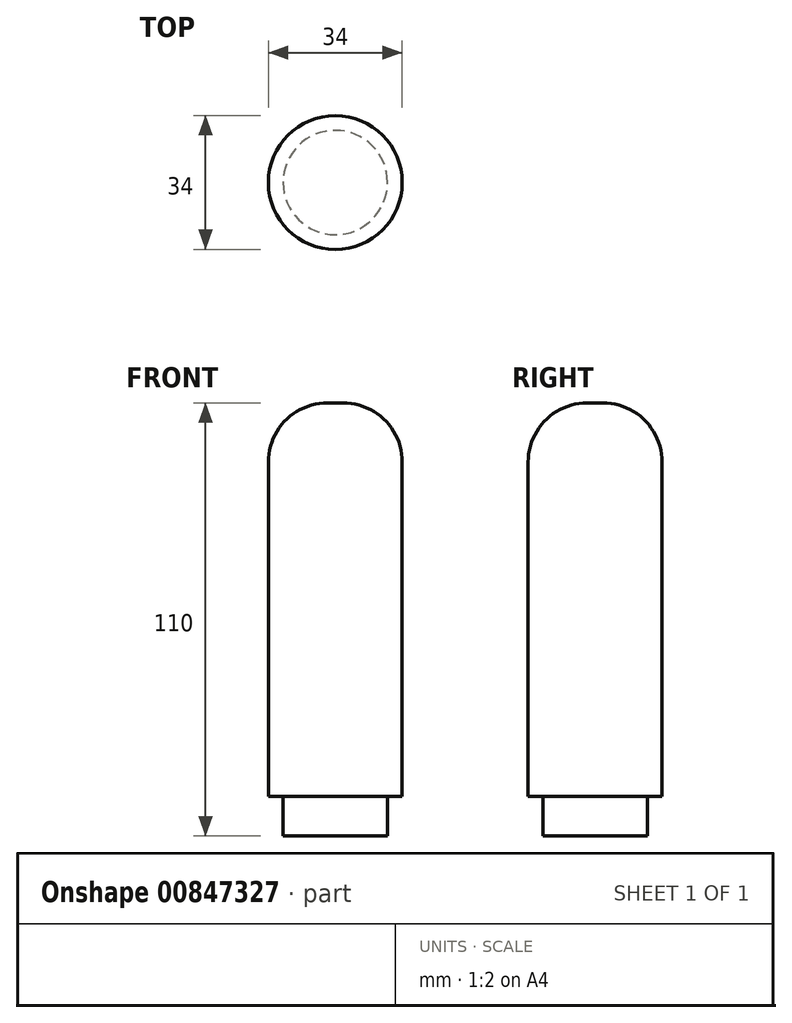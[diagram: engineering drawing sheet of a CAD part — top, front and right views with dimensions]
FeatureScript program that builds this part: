
annotation { "Feature Type Name" : "Feature", "Feature Type Description" : "" }
export const myFeature = defineFeature(function(context is Context, id is Id, definition is map)
    precondition{}
    {
        {
            var Q0;
            Q0=qCreatedBy(makeId("Top.planeOp"),FACE);
            var sketch = newSketch(context, id + "F0", { "sketchPlane" : qUnion([Q0])});
            skCircle(sketch, "E0", {"center": v(0, 0) * mm, "radius": 13.25 * mm});
            skCircle(sketch, "E1", {"center": v(0, 0) * mm, "radius": 17 * mm});
            skCircle(sketch, "E2", {"center": v(0, 0) * mm, "radius": 10.25 * mm});
            skSolve(sketch);
        }
        {
            var Q0;
            Q0 = qSketchRegion(id + "F0", true);
            var Q1;
            Q1=makeQuery(id+"F0.imprint","IMPRINT",FACE,{"disambiguationData":[TD([[makeQuery(id+"F0.imprint","IMPRINT",EDGE,{"derivedFrom":sQuery(id+"F0.wireOp",EDGE,"E0")}),1.0]])]});
            var Q2;
            Q2=makeQuery(id+"F0.imprint","IMPRINT",FACE,{"disambiguationData":[TD([[makeQuery(id+"F0.imprint","IMPRINT",EDGE,{"derivedFrom":sQuery(id+"F0.wireOp",EDGE,"E2")}),1.0]])]});
            extrude(context, id + "F1", {"entities" : qUnion([Q0, Q1, Q2]), "depth" : 100 * mm, "offsetDistance" : 25 * mm});
        }
        {
            var Q0;
            Q0=makeQuery(id+"F0.imprint","IMPRINT",FACE,{"disambiguationData":[TD([[makeQuery(id+"F0.imprint","IMPRINT",EDGE,{"derivedFrom":sQuery(id+"F0.wireOp",EDGE,"E0")}),1.0]])]});
            var Q1;
            Q1=makeQuery(id+"F0.imprint","IMPRINT",FACE,{"disambiguationData":[TD([[makeQuery(id+"F0.imprint","IMPRINT",EDGE,{"derivedFrom":sQuery(id+"F0.wireOp",EDGE,"E2")}),1.0]])]});
            extrude(context, id + "F2", {"entities" : qUnion([Q0, Q1]), "oppositeDirection" : true, "depth" : 10 * mm, "offsetDistance" : 25 * mm});
        }
        {
            var Q0;
            Q0=makeQuery(id+"F1.opExtrude","CAP_EDGE",EDGE,{"disambiguationData":[OSD([sQuery(id+"F0.wireOp",EDGE,"E1")])],"isStart":false});
            fillet(context, id + "F3", {"entities" : qUnion([Q0]), "radius" : 15 * mm, "tangentPropagation" : true, "allowEdgeOverflow" : false});
        }
    });
